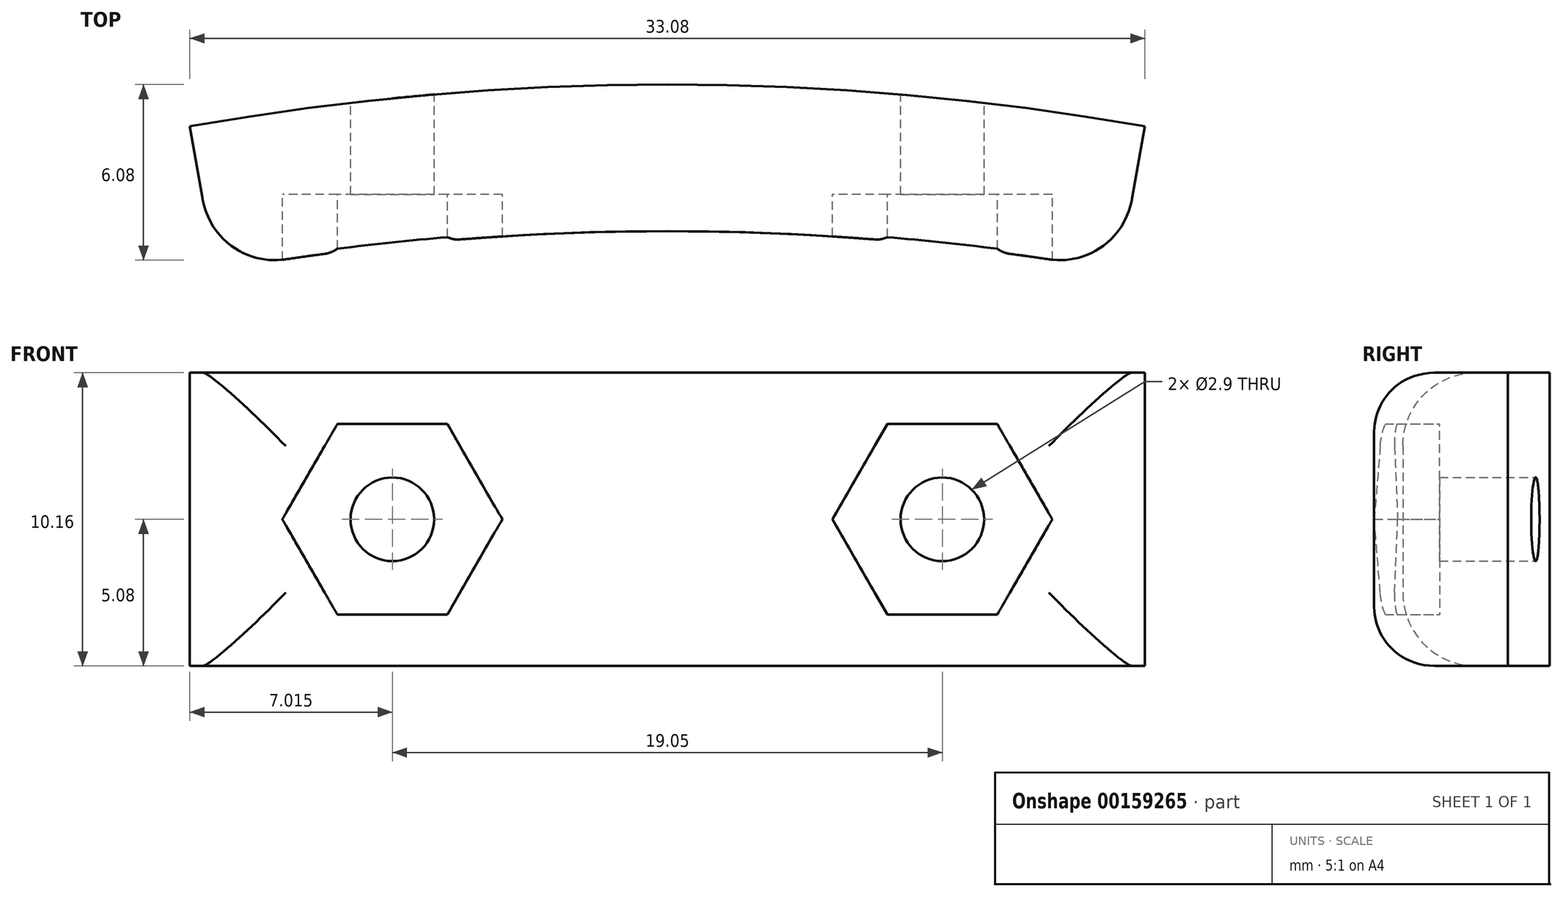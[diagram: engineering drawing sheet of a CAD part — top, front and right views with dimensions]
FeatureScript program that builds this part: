
annotation { "Feature Type Name" : "Feature", "Feature Type Description" : "" }
export const myFeature = defineFeature(function(context is Context, id is Id, definition is map)
    precondition{}
    {
        {
            var Q0;
            Q0=qCreatedBy(makeId("Top.planeOp"),FACE);
            var sketch = newSketch(context, id + "F0", { "sketchPlane" : qUnion([Q0])});
            skCircle(sketch, "E0", {"center": v(0, 0) * mm, "radius": 96.84 * mm});
            skCircle(sketch, "E1", {"center": v(0, 0) * mm, "radius": 95.25 * mm});
            skCircle(sketch, "E2", {"center": v(0, 0) * mm, "radius": 90.17 * mm});
            skLineSegment(sketch, "E3", {"start": v(0, 0) * mm, "end": v(0, 95.25) * mm});
            skLineSegment(sketch, "E4", {"start": v(0, 0) * mm, "end": v(16.54, 93.8) * mm});
            skLineSegment(sketch, "E5.MirrorCS", {"start": v(0, 0) * mm, "end": v(-16.54, 93.8) * mm});
            skSolve(sketch);
        }
        {
            var Q0;
            {var subQ0=sQuery(id+"F0.wireOp",EDGE,"E3");var subQ1=sQuery(id+"F0.wireOp",EDGE,"E1");var subQ2=makeQuery(id+"F0.imprint","INTERSECT",VERTEX,{"derivedFrom":[subQ1,subQ0]});Q0=makeQuery(id+"F0.imprint","IMPRINT",FACE,{"disambiguationData":[TD([[makeQuery(id+"F0.imprint","IMPRINT",EDGE,{"disambiguationData":[TD([[subQ2,-1.0]])],"derivedFrom":subQ1}),1.0]])]});}
            var Q1;
            {var subQ0=sQuery(id+"F0.wireOp",EDGE,"E3");var subQ1=sQuery(id+"F0.wireOp",EDGE,"E1");var subQ2=makeQuery(id+"F0.imprint","INTERSECT",VERTEX,{"derivedFrom":[subQ1,subQ0]});Q1=makeQuery(id+"F0.imprint","IMPRINT",FACE,{"disambiguationData":[TD([[makeQuery(id+"F0.imprint","IMPRINT",EDGE,{"disambiguationData":[TD([[subQ2,1.0]])],"derivedFrom":subQ1}),1.0]])]});}
            extrude(context, id + "F1", {"entities" : qUnion([Q0, Q1]), "depth" : 10.16 * mm});
        }
        {
            var Q0;
            Q0=sQuery(id+"F0.wireOp",EDGE,"E3");
            cPlane(context, id + "F2", {"entities" : qUnion([Q0]), "cplaneType" : CPlaneType.LINE_ANGLE, "offset" : 25.4 * mm, "angle" : 90 * degree, "width" : 152.4 * mm, "height" : 152.4 * mm});
        }
        {
            var Q0;
            Q0=qCreatedBy(id+"F2.planeOp",FACE);
            var sketch = newSketch(context, id + "F3", { "sketchPlane" : qUnion([Q0])});
            skLineSegment(sketch, "E6", {"start": v(95.25, 0) * mm, "end": v(95.25, 10.16) * mm});
            skSolve(sketch);
        }
        {
            var Q0;
            Q0=sQuery(id+"F3.wireOp",EDGE,"E6");
            cPlane(context, id + "F4", {"entities" : qUnion([Q0]), "cplaneType" : CPlaneType.LINE_ANGLE, "offset" : 25.4 * mm, "angle" : 90 * degree, "width" : 152.4 * mm, "height" : 152.4 * mm});
        }
        {
            var Q0;
            Q0=qCreatedBy(id+"F4.planeOp",FACE);
            var sketch = newSketch(context, id + "F5", { "sketchPlane" : qUnion([Q0])});
            skLineSegment(sketch, "E7", {"start": v(0, 0) * mm, "end": v(0, 5.08) * mm});
            skLineSegment(sketch, "E8", {"start": v(0, 5.08) * mm, "end": v(9.53, 5.08) * mm});
            skLineSegment(sketch, "E9", {"start": v(9.53, 5.08) * mm, "end": v(-9.53, 5.08) * mm});
            skCircle(sketch, "E10", {"center": v(-9.53, 5.08) * mm, "radius": 1.45 * mm});
            skCircle(sketch, "E11", {"center": v(9.53, 5.08) * mm, "radius": 1.45 * mm});
            skSolve(sketch);
        }
        {
            var Q0;
            Q0=makeQuery(id+"F5.imprint","IMPRINT",FACE,{"disambiguationData":[TD([[makeQuery(id+"F5.imprint","IMPRINT",EDGE,{"derivedFrom":sQuery(id+"F5.wireOp",EDGE,"E10")}),1.0]])]});
            var Q1;
            Q1=makeQuery(id+"F5.imprint","IMPRINT",FACE,{"disambiguationData":[TD([[makeQuery(id+"F5.imprint","IMPRINT",EDGE,{"derivedFrom":sQuery(id+"F5.wireOp",EDGE,"E11")}),1.0]])]});
            extrude(context, id + "F6", {"entities" : qUnion([Q0, Q1]), "operationType" : NewBodyOperationType.REMOVE, "oppositeDirection" : true, "depth" : 25.4 * mm});
        }
        {
            var Q0;
            Q0=qCreatedBy(id+"F2.planeOp",FACE);
            var sketch = newSketch(context, id + "F7", { "sketchPlane" : qUnion([Q0])});
            skLineSegment(sketch, "E12", {"start": v(95.25, 0) * mm, "end": v(95.25, 10.16) * mm});
            skLineSegment(sketch, "E13", {"start": v(95.25, 10.16) * mm, "end": v(90.17, 10.16) * mm});
            skLineSegment(sketch, "E14", {"start": v(90.17, 10.16) * mm, "end": v(90.17, 0) * mm});
            skSolve(sketch);
        }
        {
            var Q0;
            Q0=sQuery(id+"F7.wireOp",EDGE,"E14");
            cPlane(context, id + "F8", {"entities" : qUnion([Q0]), "cplaneType" : CPlaneType.LINE_ANGLE, "offset" : 25.4 * mm, "angle" : 90 * degree, "width" : 152.4 * mm, "height" : 152.4 * mm});
        }
        {
            var Q0;
            Q0=qCreatedBy(id+"F8.planeOp",FACE);
            var sketch = newSketch(context, id + "F9", { "sketchPlane" : qUnion([Q0])});
            skCircle(sketch, "E15.cCircle", {"center": v(9.52, 5.08) * mm, "radius": 3.81 * mm, "construction": true});
            skLineSegment(sketch, "E15.0", {"start": v(5.71, 5.08) * mm, "end": v(7.62, 8.38) * mm});
            skLineSegment(sketch, "E15.1", {"start": v(7.62, 8.38) * mm, "end": v(11.43, 8.38) * mm});
            skLineSegment(sketch, "E15.2", {"start": v(11.43, 8.38) * mm, "end": v(13.33, 5.08) * mm});
            skLineSegment(sketch, "E15.3", {"start": v(13.33, 5.08) * mm, "end": v(11.43, 1.78) * mm});
            skLineSegment(sketch, "E15.4", {"start": v(11.43, 1.78) * mm, "end": v(7.62, 1.78) * mm});
            skLineSegment(sketch, "E15.5", {"start": v(7.62, 1.78) * mm, "end": v(5.71, 5.08) * mm});
            skCircle(sketch, "E16.cCircle", {"center": v(-9.53, 5.08) * mm, "radius": 3.81 * mm, "construction": true});
            skLineSegment(sketch, "E16.0", {"start": v(-13.34, 5.08) * mm, "end": v(-11.43, 8.38) * mm});
            skLineSegment(sketch, "E16.1", {"start": v(-11.43, 8.38) * mm, "end": v(-7.62, 8.38) * mm});
            skLineSegment(sketch, "E16.2", {"start": v(-7.62, 8.38) * mm, "end": v(-5.72, 5.08) * mm});
            skLineSegment(sketch, "E16.3", {"start": v(-5.72, 5.08) * mm, "end": v(-7.62, 1.78) * mm});
            skLineSegment(sketch, "E16.4", {"start": v(-7.62, 1.78) * mm, "end": v(-11.43, 1.78) * mm});
            skLineSegment(sketch, "E16.5", {"start": v(-11.43, 1.78) * mm, "end": v(-13.34, 5.08) * mm});
            skSolve(sketch);
        }
        {
            var Q0;
            Q0=makeQuery(id+"F9.imprint","IMPRINT",FACE,{"disambiguationData":[TD([[makeQuery(id+"F9.imprint","IMPRINT",EDGE,{"derivedFrom":sQuery(id+"F9.wireOp",EDGE,"E15.0")}),-1.0]])]});
            var Q1;
            Q1=makeQuery(id+"F9.imprint","IMPRINT",FACE,{"disambiguationData":[TD([[makeQuery(id+"F9.imprint","IMPRINT",EDGE,{"derivedFrom":sQuery(id+"F9.wireOp",EDGE,"E16.0")}),-1.0]])]});
            extrude(context, id + "F10", {"entities" : qUnion([Q0, Q1]), "operationType" : NewBodyOperationType.REMOVE, "endBound" : BoundingType.SYMMETRIC, "oppositeDirection" : true, "depth" : 2.54 * mm});
        }
        {
            var Q0;
            Q0=makeQuery(id+"F1.opExtrude","CAP_EDGE",EDGE,{"disambiguationData":[OSD([sQuery(id+"F0.wireOp",EDGE,"E2")])],"isStart":false});
            var Q1;
            Q1=makeQuery(id+"F1.opExtrude","SWEPT_EDGE",EDGE,{"disambiguationData":[OSD([sQuery(id+"F0.wireOp",EDGE,"E2"),sQuery(id+"F0.wireOp",EDGE,"E4")])]});
            var Q2;
            Q2=makeQuery(id+"F1.opExtrude","CAP_EDGE",EDGE,{"disambiguationData":[OSD([sQuery(id+"F0.wireOp",EDGE,"E2")])],"isStart":true});
            var Q3;
            Q3=makeQuery(id+"F1.opExtrude","SWEPT_EDGE",EDGE,{"disambiguationData":[OSD([sQuery(id+"F0.wireOp",EDGE,"E2"),sQuery(id+"F0.wireOp",EDGE,"E5.MirrorCS")])]});
            fillet(context, id + "F11", {"entities" : qUnion([Q0, Q1, Q2, Q3]), "radius" : 2.54 * mm, "tangentPropagation" : true, "allowEdgeOverflow" : false});
        }
    });
